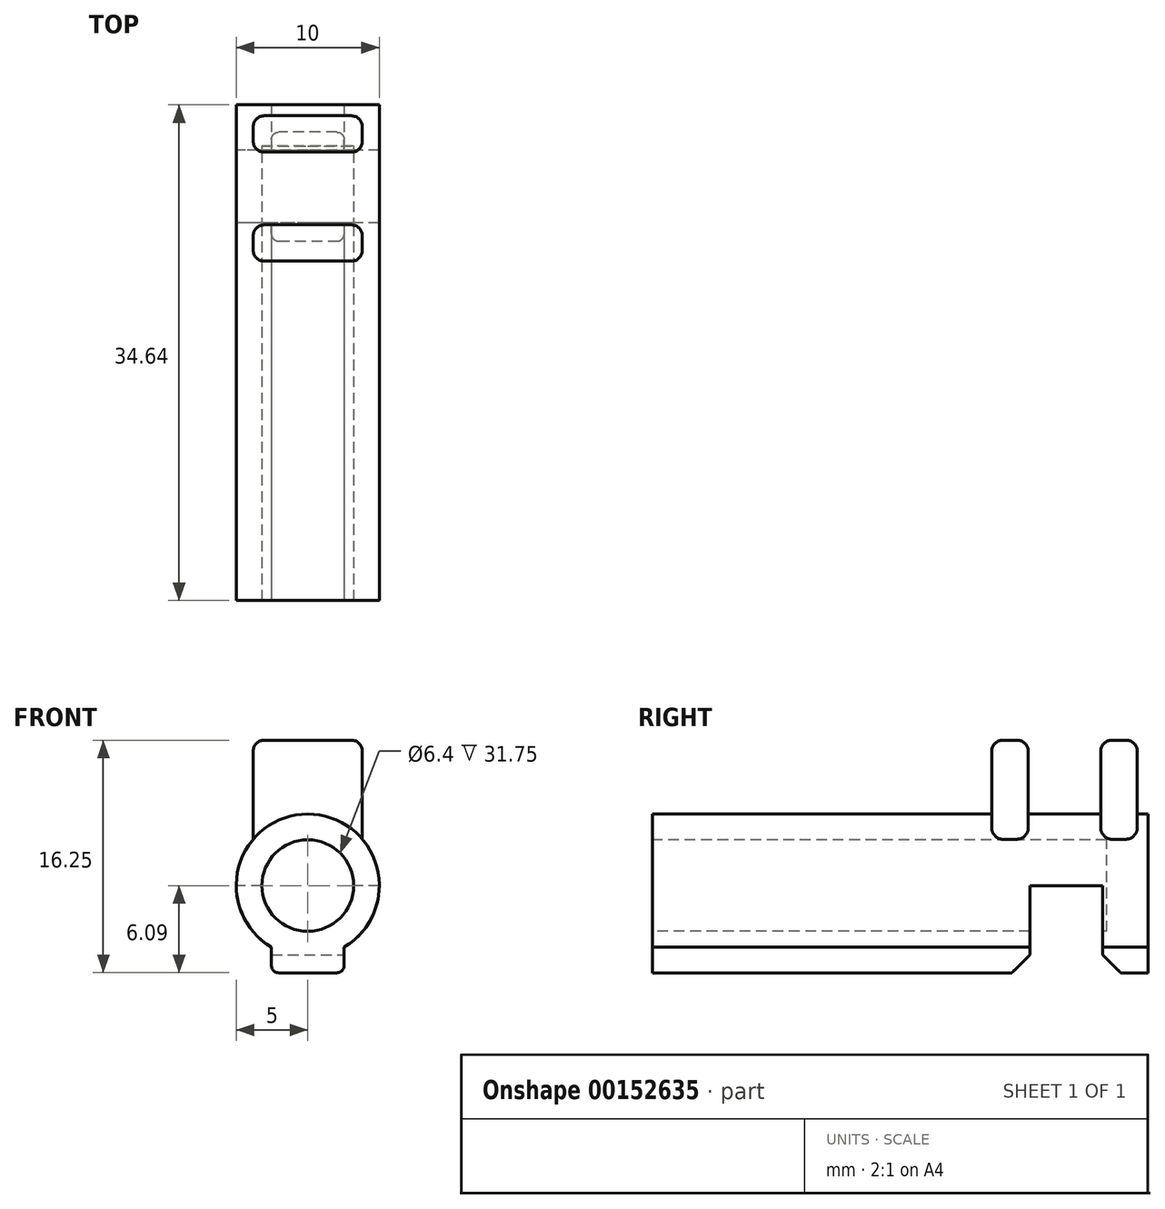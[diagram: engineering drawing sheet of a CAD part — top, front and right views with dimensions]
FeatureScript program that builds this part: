
annotation { "Feature Type Name" : "Feature", "Feature Type Description" : "" }
export const myFeature = defineFeature(function(context is Context, id is Id, definition is map)
    precondition{}
    {
        {
            var Q0;
            Q0=qCreatedBy(makeId("Top.planeOp"),FACE);
            var sketch = newSketch(context, id + "F0", { "sketchPlane" : qUnion([Q0])});
            skLineSegment(sketch, "E0", {"start": v(0, 34.64) * mm, "end": v(-30, -17.32) * mm, "construction": true});
            skLineSegment(sketch, "E1", {"start": v(-30, -17.32) * mm, "end": v(30, -17.32) * mm, "construction": true});
            skLineSegment(sketch, "E2", {"start": v(30, -17.32) * mm, "end": v(0, 34.64) * mm, "construction": true});
            skLineSegment(sketch, "E3", {"start": v(0, 34.64) * mm, "end": v(0, 0) * mm, "construction": true});
            skLineSegment(sketch, "E4", {"start": v(0, 0) * mm, "end": v(30, -17.32) * mm, "construction": true});
            skLineSegment(sketch, "E5", {"start": v(0, 0) * mm, "end": v(-30, -17.32) * mm, "construction": true});
            skSolve(sketch);
        }
        {
            var Q0;
            Q0=qCreatedBy(makeId("Front.planeOp"),FACE);
            var sketch = newSketch(context, id + "F1", { "sketchPlane" : qUnion([Q0])});
            skCircle(sketch, "E6", {"center": v(0, 0) * mm, "radius": 5 * mm});
            skSolve(sketch);
        }
        {
            var Q0;
            Q0 = qSketchRegion(id + "F1", true);
            extrude(context, id + "F2", {"entities" : qUnion([Q0]), "oppositeDirection" : true, "depth" : 34.64 * mm});
        }
        {
            var Q0;
            Q0=makeQuery(id+"F2.opExtrude","CAP_FACE",FACE,{"disambiguationData":[OSD([sQuery(id+"F1.wireOp",EDGE,"E6")])],"isStart":true});
            var sketch = newSketch(context, id + "F3", { "sketchPlane" : qUnion([Q0])});
            skLineSegment(sketch, "E7.bottom", {"start": v(-2.54, -3.2) * mm, "end": v(2.54, -3.2) * mm});
            skLineSegment(sketch, "E7.top", {"start": v(-2.54, -6.1) * mm, "end": v(2.54, -6.1) * mm});
            skLineSegment(sketch, "E7.left", {"start": v(-2.54, -3.2) * mm, "end": v(-2.54, -6.1) * mm});
            skLineSegment(sketch, "E7.right", {"start": v(2.54, -3.2) * mm, "end": v(2.54, -6.1) * mm});
            skSolve(sketch);
        }
        {
            var Q0;
            Q0 = qSketchRegion(id + "F3", true);
            var Q1;
            Q1=makeQuery(id+"F2.opExtrude","CAP_FACE",FACE,{"disambiguationData":[OSD([sQuery(id+"F1.wireOp",EDGE,"E6")])],"isStart":false});
            extrude(context, id + "F4", {"entities" : qUnion([Q0]), "operationType" : NewBodyOperationType.ADD, "endBound" : BoundingType.UP_TO_SURFACE, "oppositeDirection" : true, "endBoundEntityFace" : qUnion([Q1]), "depth" : 25.4 * mm});
        }
        {
            var Q0;
            Q0=makeQuery(id+"F2.opExtrude","CAP_FACE",FACE,{"disambiguationData":[OSD([sQuery(id+"F1.wireOp",EDGE,"E6")])],"isStart":true});
            var sketch = newSketch(context, id + "F5", { "sketchPlane" : qUnion([Q0])});
            skCircle(sketch, "E8", {"center": v(0, 0) * mm, "radius": 3.2 * mm});
            skSolve(sketch);
        }
        {
            var Q0;
            Q0=qCreatedBy(makeId("Top.planeOp"),FACE);
            var sketch = newSketch(context, id + "F6", { "sketchPlane" : qUnion([Q0])});
            skLineSegment(sketch, "E9.bottom", {"start": v(5.08, 31.47) * mm, "end": v(-5.08, 31.47) * mm});
            skLineSegment(sketch, "E9.top", {"start": v(5.08, 26.39) * mm, "end": v(-5.08, 26.39) * mm});
            skLineSegment(sketch, "E9.left", {"start": v(5.08, 31.47) * mm, "end": v(5.08, 26.39) * mm});
            skLineSegment(sketch, "E9.right", {"start": v(-5.08, 31.47) * mm, "end": v(-5.08, 26.39) * mm});
            skSolve(sketch);
        }
        {
            var Q0;
            Q0 = qSketchRegion(id + "F6", true);
            extrude(context, id + "F7", {"entities" : qUnion([Q0]), "operationType" : NewBodyOperationType.REMOVE, "oppositeDirection" : true, "depth" : 25.4 * mm});
        }
        {
            var Q0;
            Q0=qCreatedBy(makeId("Right.planeOp"),FACE);
            var sketch = newSketch(context, id + "F8", { "sketchPlane" : qUnion([Q0])});
            skLineSegment(sketch, "E10.bottom", {"start": v(33.88, 10.16) * mm, "end": v(31.34, 10.16) * mm});
            skLineSegment(sketch, "E10.top", {"start": v(33.88, 2.54) * mm, "end": v(31.34, 2.54) * mm});
            skLineSegment(sketch, "E10.left", {"start": v(33.88, 10.16) * mm, "end": v(33.88, 2.54) * mm});
            skLineSegment(sketch, "E10.right", {"start": v(31.34, 10.16) * mm, "end": v(31.34, 2.54) * mm});
            skLineSegment(sketch, "E11.bottom", {"start": v(26.26, 10.16) * mm, "end": v(23.72, 10.16) * mm});
            skLineSegment(sketch, "E11.top", {"start": v(26.26, 2.54) * mm, "end": v(23.72, 2.54) * mm});
            skLineSegment(sketch, "E11.left", {"start": v(26.26, 10.16) * mm, "end": v(26.26, 2.54) * mm});
            skLineSegment(sketch, "E11.right", {"start": v(23.72, 10.16) * mm, "end": v(23.72, 2.54) * mm});
            skSolve(sketch);
        }
        {
            var Q0;
            Q0 = qSketchRegion(id + "F8", true);
            extrude(context, id + "F9", {"entities" : qUnion([Q0]), "operationType" : NewBodyOperationType.ADD, "depth" : 3.8 * mm, "hasSecondDirection" : true, "secondDirectionOppositeDirection" : true, "secondDirectionDepth" : 3.8 * mm});
        }
        {
            var Q0;
            Q0=makeQuery(id+"F5.imprint","IMPRINT",FACE,{"disambiguationData":[TD([[makeQuery(id+"F5.imprint","IMPRINT",EDGE,{"derivedFrom":sQuery(id+"F5.wireOp",EDGE,"E8")}),1.0]])]});
            extrude(context, id + "F10", {"entities" : qUnion([Q0]), "operationType" : NewBodyOperationType.REMOVE, "oppositeDirection" : true, "depth" : 31.75 * mm});
        }
        {
            var Q0;
            Q0=makeQuery(id+"F9.opExtrude","SWEPT_EDGE",EDGE,{"disambiguationData":[OSD([sQuery(id+"F8.wireOp",EDGE,"E11.bottom"),sQuery(id+"F8.wireOp",EDGE,"E11.left")])]});
            var Q1;
            Q1=makeQuery(id+"F9.opExtrude","SWEPT_EDGE",EDGE,{"disambiguationData":[OSD([sQuery(id+"F8.wireOp",EDGE,"E10.bottom"),sQuery(id+"F8.wireOp",EDGE,"E10.right")])]});
            var Q2;
            Q2=makeQuery(id+"F9.opExtrude","SWEPT_EDGE",EDGE,{"disambiguationData":[OSD([sQuery(id+"F8.wireOp",EDGE,"E10.bottom"),sQuery(id+"F8.wireOp",EDGE,"E10.left")])]});
            var Q3;
            Q3=makeQuery(id+"F9.opExtrude","SWEPT_EDGE",EDGE,{"disambiguationData":[OSD([sQuery(id+"F8.wireOp",EDGE,"E11.bottom"),sQuery(id+"F8.wireOp",EDGE,"E11.right")])]});
            var Q4;
            Q4=makeQuery(id+"F9.opExtrude","CAP_EDGE",EDGE,{"disambiguationData":[OSD([sQuery(id+"F8.wireOp",EDGE,"E11.left")])],"isStart":true});
            var Q5;
            Q5=makeQuery(id+"F9.opExtrude","CAP_EDGE",EDGE,{"disambiguationData":[OSD([sQuery(id+"F8.wireOp",EDGE,"E11.right")])],"isStart":true});
            var Q6;
            Q6=makeQuery(id+"F9.opExtrude","CAP_EDGE",EDGE,{"disambiguationData":[OSD([sQuery(id+"F8.wireOp",EDGE,"E11.bottom")])],"isStart":true});
            var Q7;
            Q7=makeQuery(id+"F9.opExtrude","CAP_EDGE",EDGE,{"disambiguationData":[OSD([sQuery(id+"F8.wireOp",EDGE,"E10.right")])],"isStart":true});
            var Q8;
            Q8=makeQuery(id+"F9.opExtrude","CAP_EDGE",EDGE,{"disambiguationData":[OSD([sQuery(id+"F8.wireOp",EDGE,"E10.bottom")])],"isStart":true});
            var Q9;
            Q9=makeQuery(id+"F9.opExtrude","CAP_EDGE",EDGE,{"disambiguationData":[OSD([sQuery(id+"F8.wireOp",EDGE,"E10.left")])],"isStart":true});
            var Q10;
            Q10=makeQuery(id+"F9.opExtrude","CAP_EDGE",EDGE,{"disambiguationData":[OSD([sQuery(id+"F8.wireOp",EDGE,"E11.bottom")])],"isStart":false});
            var Q11;
            Q11=makeQuery(id+"F9.opExtrude","CAP_EDGE",EDGE,{"disambiguationData":[OSD([sQuery(id+"F8.wireOp",EDGE,"E11.left")])],"isStart":false});
            var Q12;
            Q12=makeQuery(id+"F9.opExtrude","CAP_EDGE",EDGE,{"disambiguationData":[OSD([sQuery(id+"F8.wireOp",EDGE,"E11.right")])],"isStart":false});
            var Q13;
            Q13=makeQuery(id+"F9.opExtrude","CAP_EDGE",EDGE,{"disambiguationData":[OSD([sQuery(id+"F8.wireOp",EDGE,"E10.right")])],"isStart":false});
            var Q14;
            Q14=makeQuery(id+"F9.opExtrude","CAP_EDGE",EDGE,{"disambiguationData":[OSD([sQuery(id+"F8.wireOp",EDGE,"E10.bottom")])],"isStart":false});
            var Q15;
            Q15=makeQuery(id+"F9.opExtrude","CAP_EDGE",EDGE,{"disambiguationData":[OSD([sQuery(id+"F8.wireOp",EDGE,"E10.left")])],"isStart":false});
            fillet(context, id + "F11", {"entities" : qUnion([Q0, Q1, Q2, Q3, Q4, Q5, Q6, Q7, Q8, Q9, Q10, Q11, Q12, Q13, Q14, Q15]), "radius" : 0.76 * mm, "tangentPropagation" : true, "allowEdgeOverflow" : false});
        }
        {
            var Q0;
            Q0=makeQuery(id+"F7.boolean.opBoolean","INTERSECT",EDGE,{"derivedFrom":[makeQuery(id+"F4.opExtrude","SWEPT_FACE",FACE,{"disambiguationData":[OSD([sQuery(id+"F3.wireOp",EDGE,"E7.top")])]}),makeQuery(id+"F7.opExtrude","SWEPT_FACE",FACE,{"disambiguationData":[OSD([sQuery(id+"F6.wireOp",EDGE,"E9.top")])]})]});
            var Q1;
            Q1=makeQuery(id+"F7.boolean.opBoolean","INTERSECT",EDGE,{"derivedFrom":[makeQuery(id+"F4.opExtrude","SWEPT_FACE",FACE,{"disambiguationData":[OSD([sQuery(id+"F3.wireOp",EDGE,"E7.top")])]}),makeQuery(id+"F7.opExtrude","SWEPT_FACE",FACE,{"disambiguationData":[OSD([sQuery(id+"F6.wireOp",EDGE,"E9.bottom")])]})]});
            chamfer(context, id + "F12", {"entities" : qUnion([Q0, Q1]), "width" : 1.27 * mm, "tangentPropagation" : true});
        }
        {
            var Q0;
            {var subQ0=sQuery(id+"F3.wireOp",EDGE,"E7.left");var subQ1=sQuery(id+"F3.wireOp",EDGE,"E7.top");Q0=makeQuery(id+"F7.boolean.opBoolean","SPLIT",EDGE,{"disambiguationData":[TD([makeQuery(id+"F2.opExtrude","CAP_FACE",FACE,{"disambiguationData":[OSD([sQuery(id+"F1.wireOp",EDGE,"E6")])],"isStart":true})])],"derivedFrom":makeQuery(id+"F4.opExtrude","SWEPT_EDGE",EDGE,{"disambiguationData":[OSD([subQ1,subQ0])]})});}
            var Q1;
            {var subQ0=sQuery(id+"F3.wireOp",EDGE,"E7.top");var subQ1=sQuery(id+"F3.wireOp",EDGE,"E7.left");Q1=makeQuery(id+"F7.boolean.opBoolean","SPLIT",EDGE,{"disambiguationData":[TD([makeQuery(id+"F2.opExtrude","CAP_FACE",FACE,{"disambiguationData":[OSD([sQuery(id+"F1.wireOp",EDGE,"E6")])],"isStart":false})])],"derivedFrom":makeQuery(id+"F4.opExtrude","SWEPT_EDGE",EDGE,{"disambiguationData":[OSD([subQ0,subQ1])]})});}
            var Q2;
            {var subQ0=sQuery(id+"F3.wireOp",EDGE,"E7.right");var subQ1=sQuery(id+"F3.wireOp",EDGE,"E7.top");Q2=makeQuery(id+"F7.boolean.opBoolean","SPLIT",EDGE,{"disambiguationData":[TD([makeQuery(id+"F2.opExtrude","CAP_FACE",FACE,{"disambiguationData":[OSD([sQuery(id+"F1.wireOp",EDGE,"E6")])],"isStart":false})])],"derivedFrom":makeQuery(id+"F4.opExtrude","SWEPT_EDGE",EDGE,{"disambiguationData":[OSD([subQ1,subQ0])]})});}
            var Q3;
            {var subQ0=sQuery(id+"F3.wireOp",EDGE,"E7.right");var subQ1=sQuery(id+"F3.wireOp",EDGE,"E7.top");Q3=makeQuery(id+"F7.boolean.opBoolean","SPLIT",EDGE,{"disambiguationData":[TD([makeQuery(id+"F2.opExtrude","CAP_FACE",FACE,{"disambiguationData":[OSD([sQuery(id+"F1.wireOp",EDGE,"E6")])],"isStart":true})])],"derivedFrom":makeQuery(id+"F4.opExtrude","SWEPT_EDGE",EDGE,{"disambiguationData":[OSD([subQ1,subQ0])]})});}
            fillet(context, id + "F13", {"entities" : qUnion([Q0, Q1, Q2, Q3]), "radius" : 0.5 * mm, "tangentPropagation" : true, "allowEdgeOverflow" : false});
        }
    });
